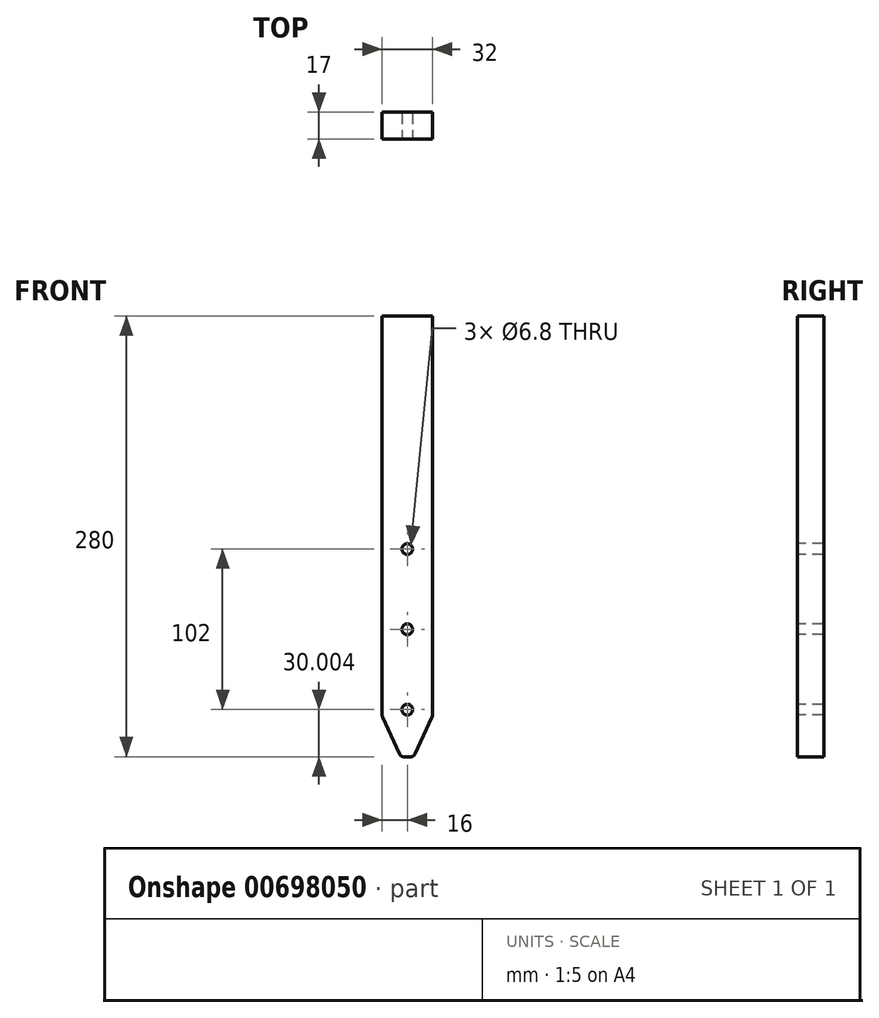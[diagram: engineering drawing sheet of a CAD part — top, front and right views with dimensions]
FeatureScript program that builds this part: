
annotation { "Feature Type Name" : "Feature", "Feature Type Description" : "" }
export const myFeature = defineFeature(function(context is Context, id is Id, definition is map)
    precondition{}
    {
        {
            var Q0;
            Q0=qCreatedBy(makeId("Front.planeOp"),FACE);
            var sketch = newSketch(context, id + "F0", { "sketchPlane" : qUnion([Q0])});
            skLineSegment(sketch, "E0.bottom", {"start": v(-16, 159.5) * mm, "end": v(0, 159.5) * mm});
            skLineSegment(sketch, "E0.left", {"start": v(-16, 159.5) * mm, "end": v(-16, -93.85) * mm});
            skPoint(sketch, "E0.middle", {"position": v(0, 0) * mm});
            skLineSegment(sketch, "E1", {"start": v(0, 168.5) * mm, "end": v(0, -147.15) * mm, "construction": true});
            skLineSegment(sketch, "E2", {"start": v(-2.08, -120.5) * mm, "end": v(0, -120.5) * mm});
            skLineSegment(sketch, "E3", {"start": v(-15.72, -95.1) * mm, "end": v(-4.8, -118.76) * mm});
            skPoint(sketch, "E4.visualSharp", {"position": v(-4, -120.5) * mm});
            skArc(sketch, "E4.filletArc", {"start": v(-4.8, -118.76) * mm, "mid": v(-3.7, -120.03) * mm, "end": v(-2.08, -120.5) * mm});
            skPoint(sketch, "E5.visualSharp", {"position": v(-16, -94.5) * mm});
            skArc(sketch, "E5.filletArc", {"start": v(-16, -93.85) * mm, "mid": v(-15.93, -94.5) * mm, "end": v(-15.72, -95.1) * mm});
            skLineSegment(sketch, "E6.MirrorCS", {"start": v(0, 150.48) * mm, "end": v(0, 168.5) * mm, "construction": true});
            skLineSegment(sketch, "E7.MirrorCS", {"start": v(16, 159.5) * mm, "end": v(16, -93.85) * mm});
            skArc(sketch, "E8.MirrorCS", {"start": v(16, -93.85) * mm, "mid": v(15.93, -94.5) * mm, "end": v(15.72, -95.1) * mm});
            skLineSegment(sketch, "E9.MirrorCS", {"start": v(15.72, -95.1) * mm, "end": v(4.8, -118.76) * mm});
            skArc(sketch, "E10.MirrorCS", {"start": v(4.8, -118.76) * mm, "mid": v(3.7, -120.03) * mm, "end": v(2.08, -120.5) * mm});
            skLineSegment(sketch, "E11.MirrorCS", {"start": v(2.08, -120.5) * mm, "end": v(0, -120.5) * mm});
            skLineSegment(sketch, "E12.MirrorCS", {"start": v(16, 159.5) * mm, "end": v(0, 159.5) * mm});
            skSolve(sketch);
        }
        {
            var Q0;
            Q0 = qSketchRegion(id + "F0", true);
            extrude(context, id + "F1", {"entities" : qUnion([Q0]), "depth" : 17 * mm, "offsetDistance" : 25 * mm});
        }
        {
            var Q0;
            Q0=makeQuery(id+"F1.opExtrude","CAP_FACE",FACE,{"disambiguationData":[OSD([sQuery(id+"F0.wireOp",EDGE,"E0.bottom"),sQuery(id+"F0.wireOp",EDGE,"E0.left"),sQuery(id+"F0.wireOp",EDGE,"E2"),sQuery(id+"F0.wireOp",EDGE,"E3"),sQuery(id+"F0.wireOp",EDGE,"E4.filletArc"),sQuery(id+"F0.wireOp",EDGE,"E5.filletArc"),sQuery(id+"F0.wireOp",EDGE,"E7.MirrorCS"),sQuery(id+"F0.wireOp",EDGE,"E8.MirrorCS"),sQuery(id+"F0.wireOp",EDGE,"E9.MirrorCS"),sQuery(id+"F0.wireOp",EDGE,"E10.MirrorCS"),sQuery(id+"F0.wireOp",EDGE,"E11.MirrorCS"),sQuery(id+"F0.wireOp",EDGE,"E12.MirrorCS")])],"isStart":false});
            var sketch = newSketch(context, id + "F2", { "sketchPlane" : qUnion([Q0])});
            skPoint(sketch, "E13", {"position": v(0, -90.5) * mm});
            skPoint(sketch, "E14", {"position": v(0, -39.5) * mm});
            skPoint(sketch, "E15", {"position": v(0, 11.5) * mm});
            skSolve(sketch);
        }
        {
            var Q0;
            Q0=sQuery(id+"F2.wireOp",VERTEX,"E15");
            var Q1;
            Q1=sQuery(id+"F2.wireOp",VERTEX,"E14");
            var Q2;
            Q2=sQuery(id+"F2.wireOp",VERTEX,"E13");
            var Q3;
            Q3=makeQuery(id+"F1.opExtrude","SWEPT_BODY",BODY,{"disambiguationData":[OSD([sQuery(id+"F0.wireOp",EDGE,"E0.bottom"),sQuery(id+"F0.wireOp",EDGE,"E0.left"),sQuery(id+"F0.wireOp",EDGE,"E2"),sQuery(id+"F0.wireOp",EDGE,"E3"),sQuery(id+"F0.wireOp",EDGE,"E4.filletArc"),sQuery(id+"F0.wireOp",EDGE,"E5.filletArc"),sQuery(id+"F0.wireOp",EDGE,"E7.MirrorCS"),sQuery(id+"F0.wireOp",EDGE,"E8.MirrorCS"),sQuery(id+"F0.wireOp",EDGE,"E9.MirrorCS"),sQuery(id+"F0.wireOp",EDGE,"E10.MirrorCS"),sQuery(id+"F0.wireOp",EDGE,"E11.MirrorCS"),sQuery(id+"F0.wireOp",EDGE,"E12.MirrorCS")])]});
            hole(context, id + "F3", {"style" : HoleStyle.SIMPLE, "endStyle" : HoleEndStyle.THROUGH, "standardTappedOrClearance" : lookupTablePath({ "standard" : "ISO", "engagement" : "75%", "pitch" : "1.25 mm", "size" : "M8", "type" : "Tapped" }), "standardBlindInLast" : lookupTablePath({ "standard" : "ISO", "engagement" : "75%", "pitch" : "1.25 mm", "size" : "M8", "type" : "Tapped" }), "holeDiameter" : 6.8 * mm, "majorDiameter" : 8 * mm, "showTappedDepth" : true, "isTappedThrough" : true, "tappedDepth" : 16.25 * mm, "tapClearance" : 3, "locations" : qUnion([Q0, Q1, Q2]), "scope" : qUnion([Q3])});
        }
    });
